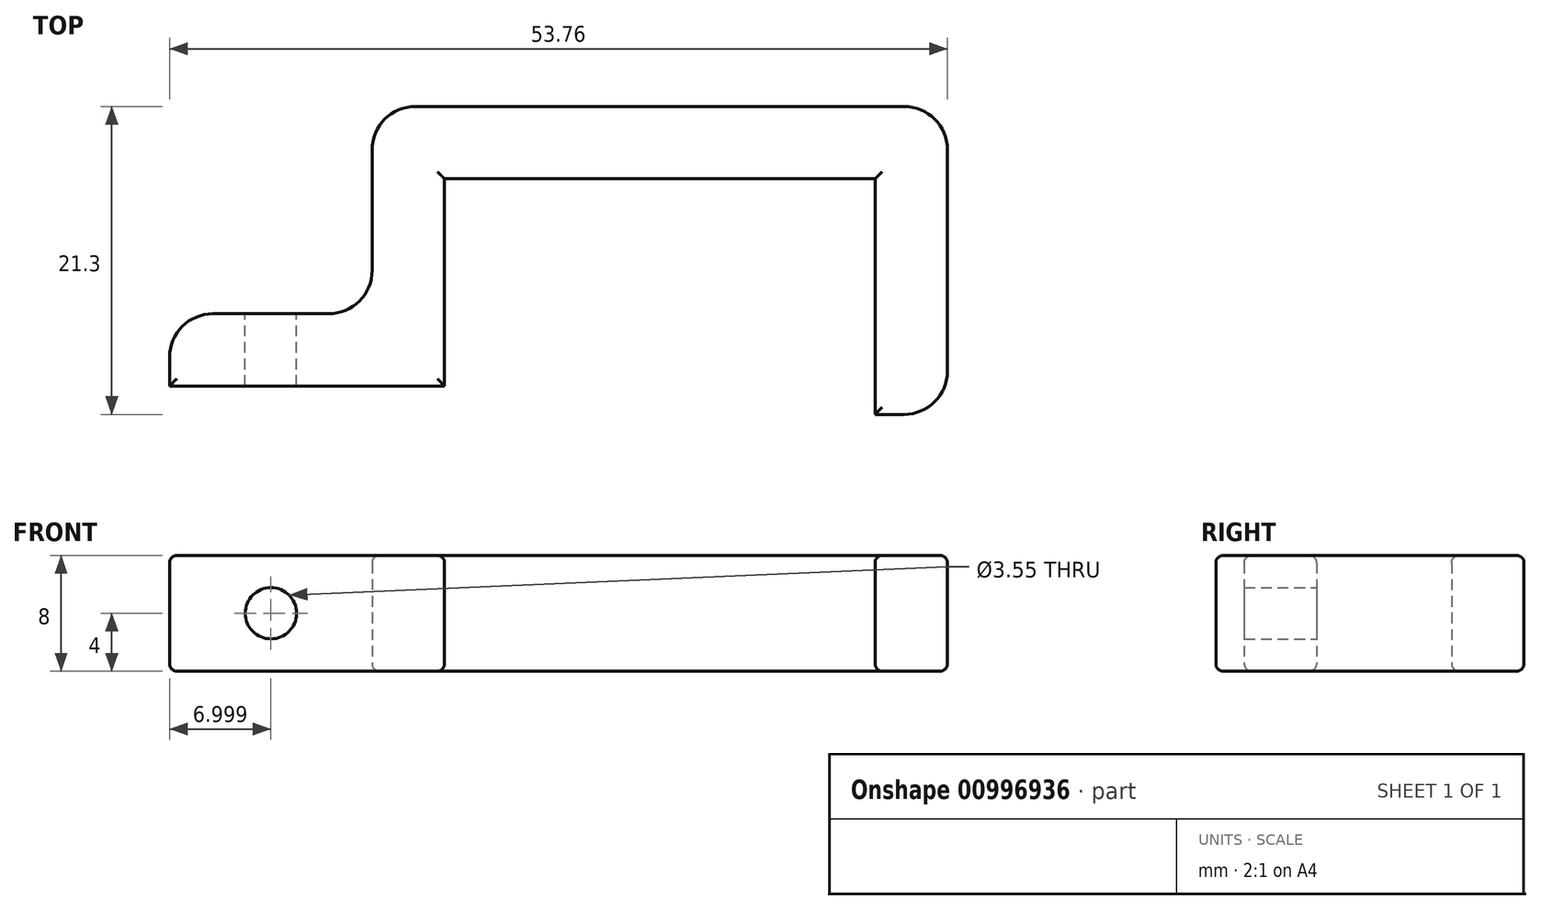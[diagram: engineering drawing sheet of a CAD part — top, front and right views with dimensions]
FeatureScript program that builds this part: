
annotation { "Feature Type Name" : "Feature", "Feature Type Description" : "" }
export const myFeature = defineFeature(function(context is Context, id is Id, definition is map)
    precondition{}
    {
        {
            var Q0;
            Q0=qCreatedBy(makeId("Top.planeOp"),FACE);
            var sketch = newSketch(context, id + "F0", { "sketchPlane" : qUnion([Q0])});
            skLineSegment(sketch, "E0", {"start": v(-33.88, 0) * mm, "end": v(-14.88, 0) * mm});
            skLineSegment(sketch, "E1", {"start": v(-14.88, 0) * mm, "end": v(-14.88, 14.33) * mm});
            skLineSegment(sketch, "E2", {"start": v(-14.88, 14.33) * mm, "end": v(14.88, 14.33) * mm});
            skLineSegment(sketch, "E3", {"start": v(14.88, 14.33) * mm, "end": v(14.88, -1.97) * mm});
            skLineSegment(sketch, "E4", {"start": v(14.88, -1.97) * mm, "end": v(16.88, -1.97) * mm});
            skLineSegment(sketch, "E5", {"start": v(19.88, 1.03) * mm, "end": v(19.88, 16.33) * mm});
            skLineSegment(sketch, "E6", {"start": v(16.88, 19.33) * mm, "end": v(-16.88, 19.33) * mm});
            skLineSegment(sketch, "E7", {"start": v(-19.88, 16.33) * mm, "end": v(-19.88, 8) * mm});
            skLineSegment(sketch, "E8", {"start": v(-22.88, 5) * mm, "end": v(-30.88, 5) * mm});
            skLineSegment(sketch, "E9", {"start": v(-33.88, 2) * mm, "end": v(-33.88, 0) * mm});
            skLineSegment(sketch, "E10", {"start": v(-19.88, 5) * mm, "end": v(-14.88, 0) * mm, "construction": true});
            skLineSegment(sketch, "E11", {"start": v(-19.88, 19.33) * mm, "end": v(-14.88, 14.33) * mm, "construction": true});
            skLineSegment(sketch, "E12", {"start": v(19.88, 19.33) * mm, "end": v(14.88, 14.33) * mm, "construction": true});
            skPoint(sketch, "E13.visualSharp", {"position": v(-19.88, 5) * mm});
            skArc(sketch, "E13.filletArc", {"start": v(-22.88, 5) * mm, "mid": v(-20.76, 5.88) * mm, "end": v(-19.88, 8) * mm});
            skPoint(sketch, "E14.visualSharp", {"position": v(-19.88, 19.33) * mm});
            skArc(sketch, "E14.filletArc", {"start": v(-16.88, 19.33) * mm, "mid": v(-19, 18.46) * mm, "end": v(-19.88, 16.33) * mm});
            skPoint(sketch, "E15.visualSharp", {"position": v(19.88, 19.33) * mm});
            skArc(sketch, "E15.filletArc", {"start": v(19.88, 16.33) * mm, "mid": v(19, 18.46) * mm, "end": v(16.88, 19.33) * mm});
            skPoint(sketch, "E16.visualSharp", {"position": v(19.88, -1.97) * mm});
            skArc(sketch, "E16.filletArc", {"start": v(16.88, -1.97) * mm, "mid": v(19, -1.09) * mm, "end": v(19.88, 1.03) * mm});
            skPoint(sketch, "E17.visualSharp", {"position": v(-33.88, 5) * mm});
            skArc(sketch, "E17.filletArc", {"start": v(-30.88, 5) * mm, "mid": v(-33, 4.12) * mm, "end": v(-33.88, 2) * mm});
            skSolve(sketch);
        }
        {
            var Q0;
            Q0=makeQuery(id+"F0.imprint","IMPRINT",FACE,{"disambiguationData":[TD([[makeQuery(id+"F0.imprint","IMPRINT",EDGE,{"derivedFrom":sQuery(id+"F0.wireOp",EDGE,"E0")}),1.0]])]});
            extrude(context, id + "F1", {"entities" : qUnion([Q0]), "endBound" : BoundingType.SYMMETRIC, "depth" : 8 * mm, "offsetDistance" : 25 * mm});
        }
        {
            var Q0;
            Q0=makeQuery(id+"F1.opExtrude","SWEPT_FACE",FACE,{"disambiguationData":[OSD([sQuery(id+"F0.wireOp",EDGE,"E8")])]});
            var sketch = newSketch(context, id + "F2", { "sketchPlane" : qUnion([Q0])});
            skCircle(sketch, "E18", {"center": v(26.88, 0) * mm, "radius": 1.78 * mm});
            skPoint(sketch, "E18.centerSnap0", {"position": v(26.88, 4) * mm});
            skPoint(sketch, "E18.centerSnap1", {"position": v(34.16, 0) * mm});
            skSolve(sketch);
        }
        {
            var Q0;
            Q0=makeQuery(id+"F2.imprint","IMPRINT",FACE,{"disambiguationData":[TD([[makeQuery(id+"F2.imprint","IMPRINT",EDGE,{"derivedFrom":sQuery(id+"F2.wireOp",EDGE,"E18")}),1.0]])]});
            extrude(context, id + "F3", {"entities" : qUnion([Q0]), "operationType" : NewBodyOperationType.REMOVE, "endBound" : BoundingType.THROUGH_ALL, "oppositeDirection" : true, "depth" : 25 * mm, "offsetDistance" : 25 * mm});
        }
        {
            var Q0;
            Q0=makeQuery(id+"F1.opExtrude","CAP_FACE",FACE,{"disambiguationData":[OSD([sQuery(id+"F0.wireOp",EDGE,"E0"),sQuery(id+"F0.wireOp",EDGE,"E1"),sQuery(id+"F0.wireOp",EDGE,"E2"),sQuery(id+"F0.wireOp",EDGE,"E3"),sQuery(id+"F0.wireOp",EDGE,"E4"),sQuery(id+"F0.wireOp",EDGE,"E5"),sQuery(id+"F0.wireOp",EDGE,"E6"),sQuery(id+"F0.wireOp",EDGE,"E7"),sQuery(id+"F0.wireOp",EDGE,"E8"),sQuery(id+"F0.wireOp",EDGE,"E9"),sQuery(id+"F0.wireOp",EDGE,"E13.filletArc"),sQuery(id+"F0.wireOp",EDGE,"E14.filletArc"),sQuery(id+"F0.wireOp",EDGE,"E15.filletArc"),sQuery(id+"F0.wireOp",EDGE,"E16.filletArc"),sQuery(id+"F0.wireOp",EDGE,"E17.filletArc")])],"isStart":false});
            var Q1;
            Q1=makeQuery(id+"F1.opExtrude","CAP_FACE",FACE,{"disambiguationData":[OSD([sQuery(id+"F0.wireOp",EDGE,"E0"),sQuery(id+"F0.wireOp",EDGE,"E1"),sQuery(id+"F0.wireOp",EDGE,"E2"),sQuery(id+"F0.wireOp",EDGE,"E3"),sQuery(id+"F0.wireOp",EDGE,"E4"),sQuery(id+"F0.wireOp",EDGE,"E5"),sQuery(id+"F0.wireOp",EDGE,"E6"),sQuery(id+"F0.wireOp",EDGE,"E7"),sQuery(id+"F0.wireOp",EDGE,"E8"),sQuery(id+"F0.wireOp",EDGE,"E9"),sQuery(id+"F0.wireOp",EDGE,"E13.filletArc"),sQuery(id+"F0.wireOp",EDGE,"E14.filletArc"),sQuery(id+"F0.wireOp",EDGE,"E15.filletArc"),sQuery(id+"F0.wireOp",EDGE,"E16.filletArc"),sQuery(id+"F0.wireOp",EDGE,"E17.filletArc")])],"isStart":true});
            fillet(context, id + "F4", {"entities" : qUnion([Q0, Q1]), "radius" : 0.5 * mm, "tangentPropagation" : true, "allowEdgeOverflow" : false});
        }
    });
